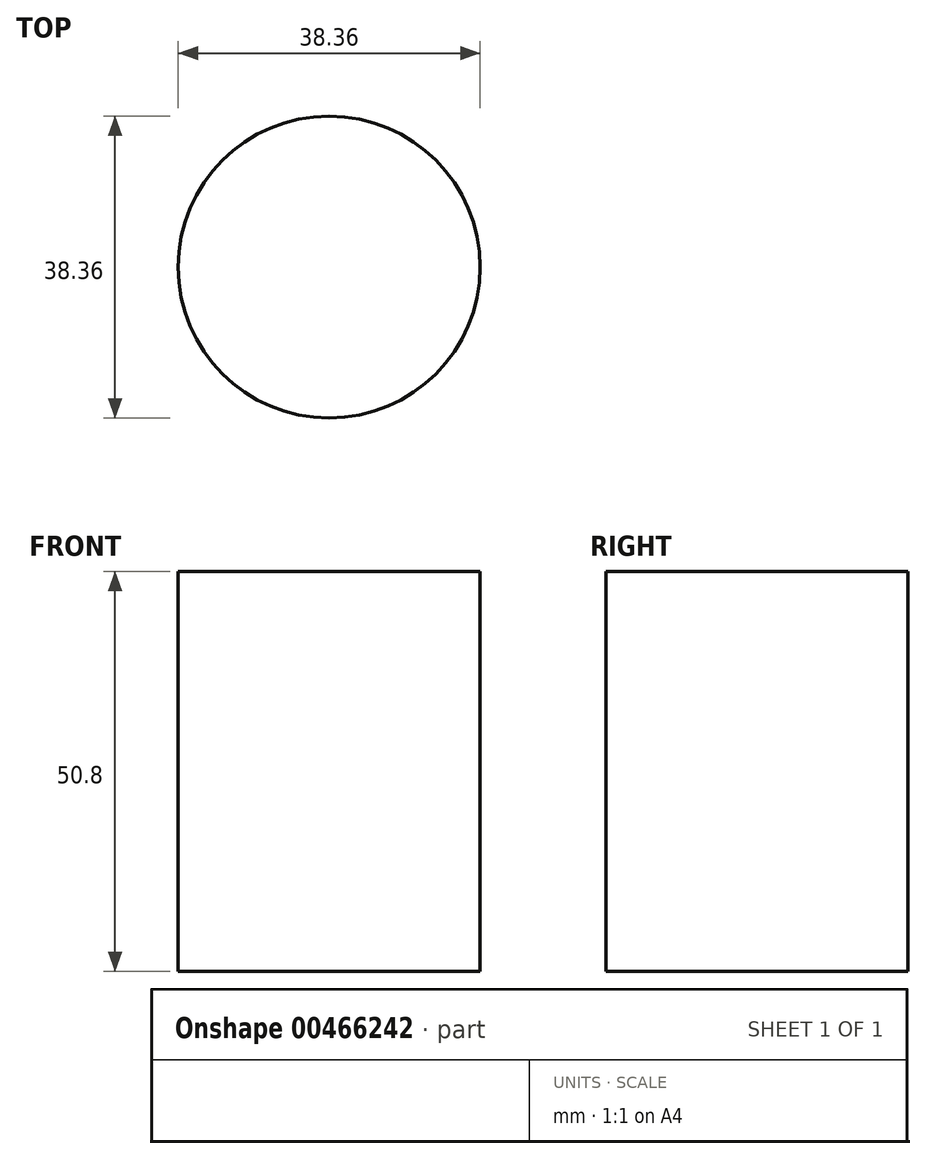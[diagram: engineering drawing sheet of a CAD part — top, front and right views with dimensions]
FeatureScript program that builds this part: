
annotation { "Feature Type Name" : "Feature", "Feature Type Description" : "" }
export const myFeature = defineFeature(function(context is Context, id is Id, definition is map)
    precondition{}
    {
        {
            var Q0;
            Q0=qCreatedBy(makeId("Top.planeOp"),FACE);
            var sketch = newSketch(context, id + "F0", { "sketchPlane" : qUnion([Q0])});
            skCircle(sketch, "E0", {"center": v(0, 0) * mm, "radius": 19.18 * mm});
            skSolve(sketch);
        }
        {
            var Q0;
            Q0 = qSketchRegion(id + "F0", true);
            extrude(context, id + "F1", {"entities" : qUnion([Q0]), "depth" : 50.8 * mm});
        }
    });
